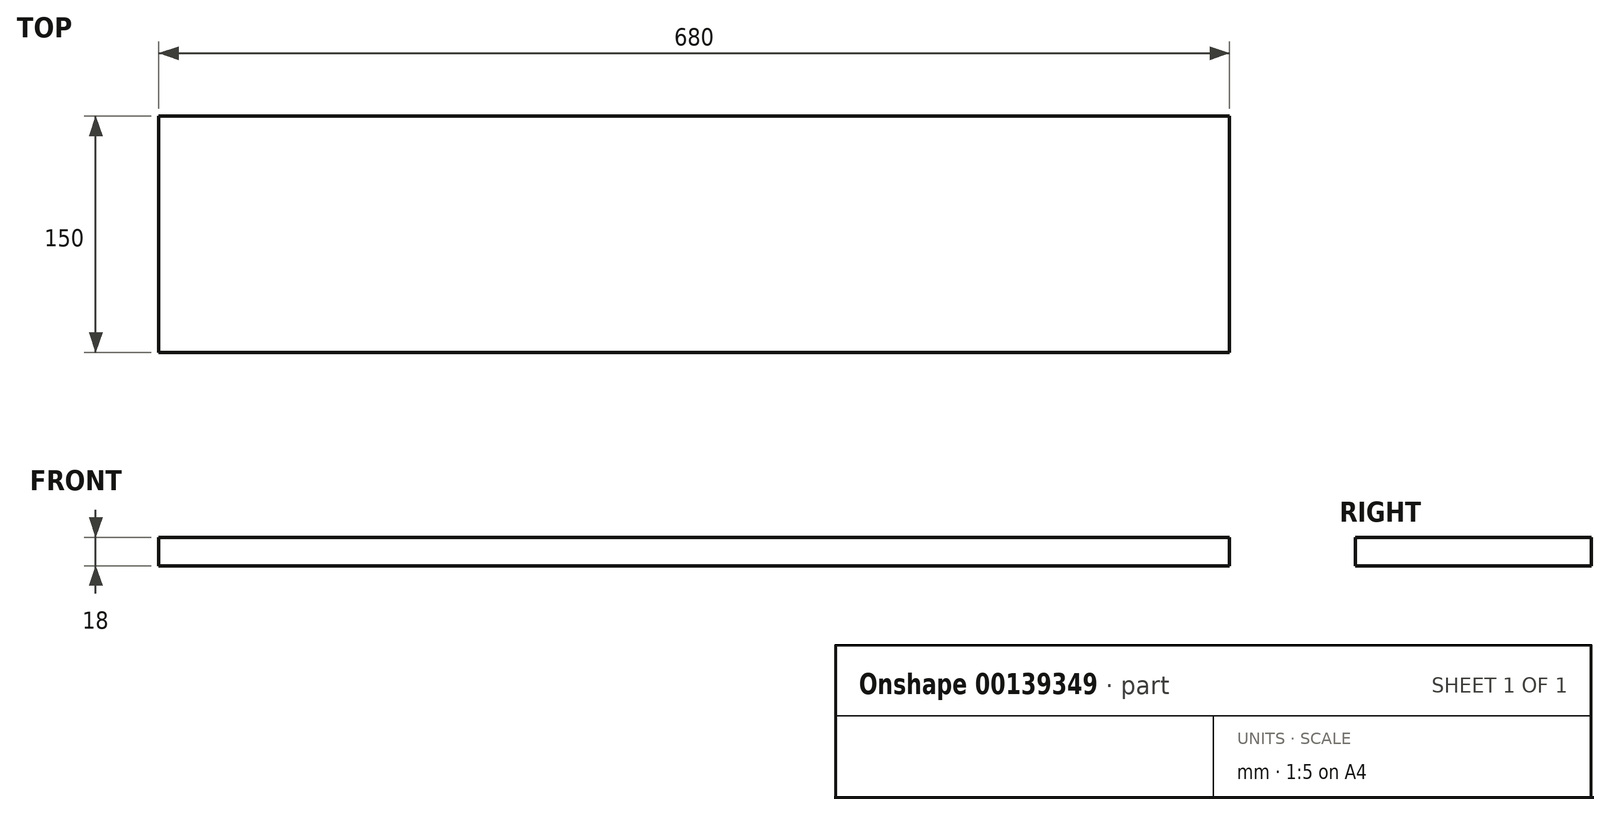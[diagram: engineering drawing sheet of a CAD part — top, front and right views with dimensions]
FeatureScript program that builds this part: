
annotation { "Feature Type Name" : "Feature", "Feature Type Description" : "" }
export const myFeature = defineFeature(function(context is Context, id is Id, definition is map)
    precondition{}
    {
        {
            assignVariable(context, id + "F0", {"name" : "T", "anyValue" : 18});
        }
        {
            var Q0;
            Q0=qCreatedBy(makeId("Top.planeOp"),FACE);
            var sketch = newSketch(context, id + "F1", { "sketchPlane" : qUnion([Q0])});
            skLineSegment(sketch, "E0.bottom", {"start": v(0, 0) * mm, "end": v(680, 0) * mm});
            skLineSegment(sketch, "E0.top", {"start": v(0, 150) * mm, "end": v(680, 150) * mm});
            skLineSegment(sketch, "E0.left", {"start": v(0, 0) * mm, "end": v(0, 150) * mm});
            skLineSegment(sketch, "E0.right", {"start": v(680, 0) * mm, "end": v(680, 150) * mm});
            skSolve(sketch);
        }
        {
            var Q0;
            Q0=makeQuery(id+"F1.imprint","IMPRINT",FACE,{"disambiguationData":[TD([[makeQuery(id+"F1.imprint","IMPRINT",EDGE,{"derivedFrom":sQuery(id+"F1.wireOp",EDGE,"E0.bottom")}),1.0]])]});
            extrude(context, id + "F2", {"entities" : qUnion([Q0]), "depth" : (getVariable(context, 'T')) * mm});
        }
    });
